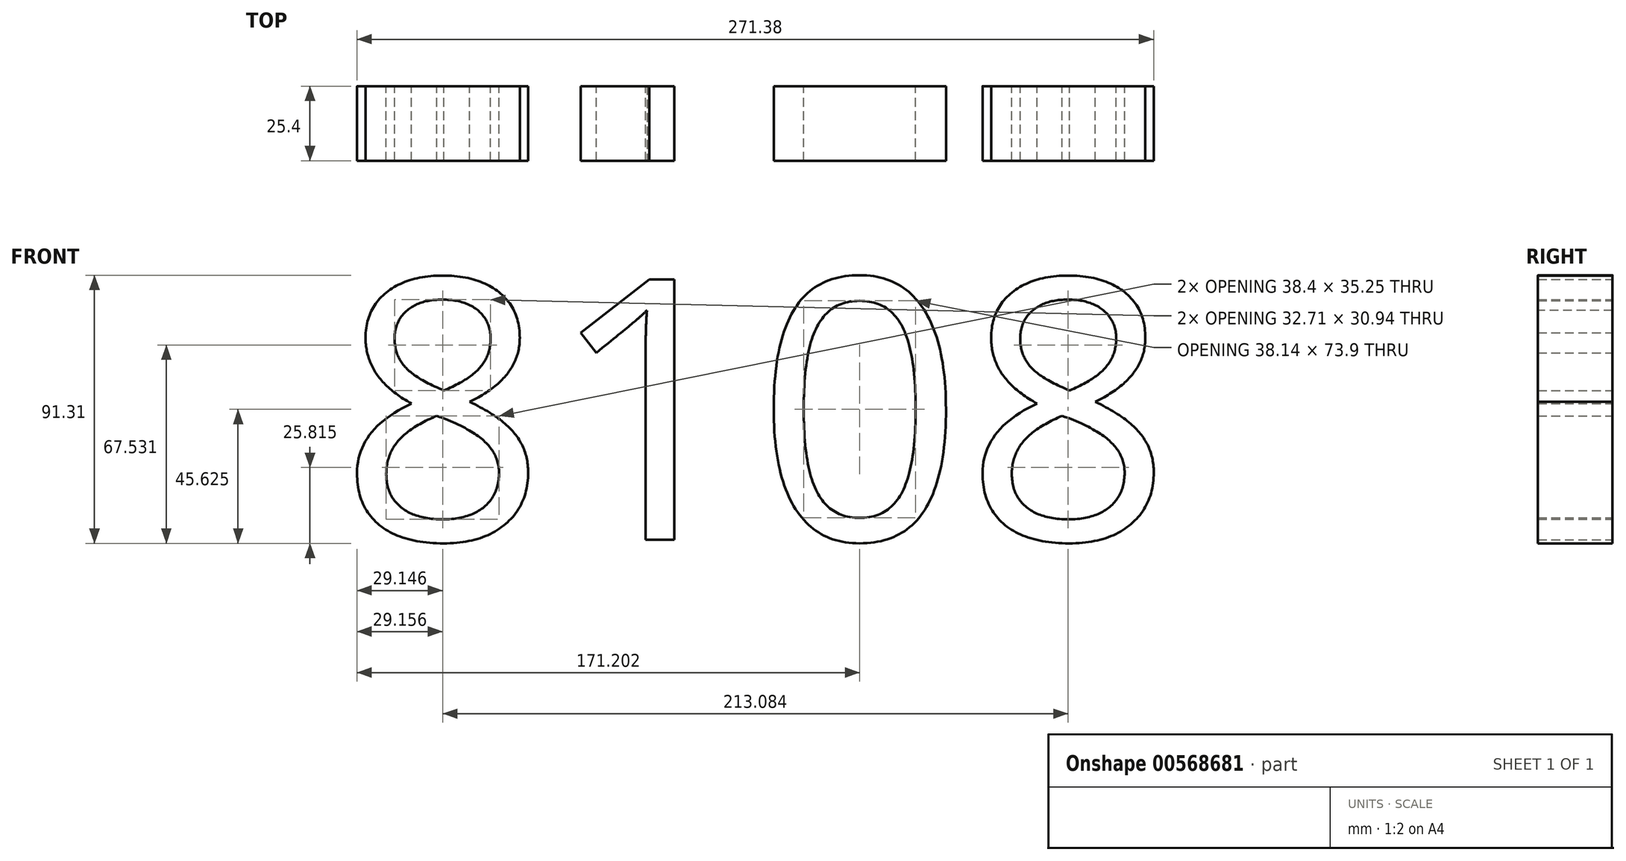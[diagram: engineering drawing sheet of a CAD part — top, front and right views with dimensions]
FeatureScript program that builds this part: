
annotation { "Feature Type Name" : "Feature", "Feature Type Description" : "" }
export const myFeature = defineFeature(function(context is Context, id is Id, definition is map)
    precondition{}
    {
        {
            var Q0;
            Q0=qCreatedBy(makeId("Front.planeOp"),FACE);
            var sketch = newSketch(context, id + "F0", { "sketchPlane" : qUnion([Q0])});
            skText(sketch, "E0", { "text": "8108", "fontName": "OpenSans-Regular.ttf"});
            const initialGuessF0  = {"E0": [-0.20571, -0.03548, 1, 0, 0.08945]};
            skSetInitialGuess(sketch, initialGuessF0);
            skSolve(sketch);
        }
        {
            var Q0;
            Q0=makeQuery(id+"F0.imprint","IMPRINT",FACE,{"disambiguationData":[TD([[makeQuery(id+"F0.imprint","IMPRINT",EDGE,{"derivedFrom":sQuery(id+"F0.wireOp",EDGE,"E0.sketch_text.stroke-0")}),-1.0]])]});
            var Q1;
            Q1=makeQuery(id+"F0.imprint","IMPRINT",FACE,{"disambiguationData":[TD([[makeQuery(id+"F0.imprint","IMPRINT",EDGE,{"derivedFrom":sQuery(id+"F0.wireOp",EDGE,"E0.sketch_text.stroke-31")}),-1.0]])]});
            var Q2;
            Q2=makeQuery(id+"F0.imprint","IMPRINT",FACE,{"disambiguationData":[TD([[makeQuery(id+"F0.imprint","IMPRINT",EDGE,{"derivedFrom":sQuery(id+"F0.wireOp",EDGE,"E0.sketch_text.stroke-40")}),-1.0]])]});
            var Q3;
            Q3=makeQuery(id+"F0.imprint","IMPRINT",FACE,{"disambiguationData":[TD([[makeQuery(id+"F0.imprint","IMPRINT",EDGE,{"derivedFrom":sQuery(id+"F0.wireOp",EDGE,"E0.sketch_text.stroke-56")}),-1.0]])]});
            extrude(context, id + "F1", {"entities" : qUnion([Q0, Q1, Q2, Q3]), "depth" : 25.4 * mm, "offsetDistance" : 25.4 * mm});
        }
    });
